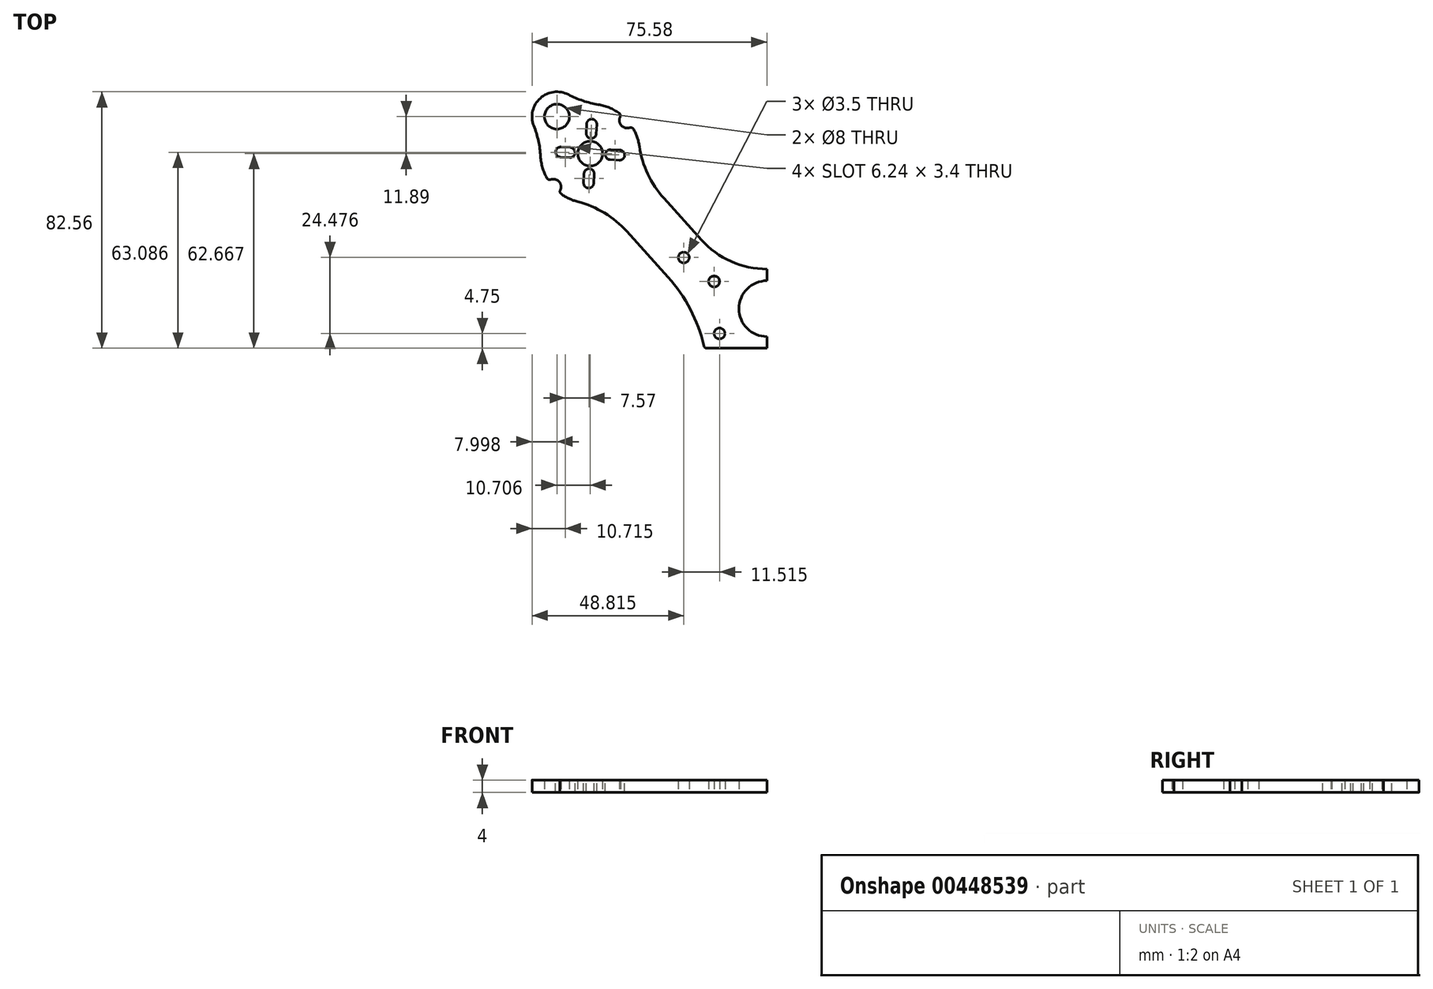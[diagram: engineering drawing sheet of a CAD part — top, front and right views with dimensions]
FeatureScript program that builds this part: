
annotation { "Feature Type Name" : "Feature", "Feature Type Description" : "" }
export const myFeature = defineFeature(function(context is Context, id is Id, definition is map)
    precondition{}
    {
        {
            var Q0;
            Q0=qCreatedBy(makeId("Top.planeOp"),FACE);
            var sketch = newSketch(context, id + "F0", { "sketchPlane" : qUnion([Q0])});
            skLineSegment(sketch, "E0", {"start": v(0, 10) * mm, "end": v(-56.88, 73.17) * mm, "construction": true});
            skCircle(sketch, "E1", {"center": v(-17, 32) * mm, "radius": 1.75 * mm});
            skCircle(sketch, "E2", {"center": v(-15.25, 15.25) * mm, "radius": 1.75 * mm});
            skLineSegment(sketch, "E3", {"start": v(-45.07, 48.1) * mm, "end": v(-31.81, 33.37) * mm});
            skLineSegment(sketch, "E4", {"start": v(-33.18, 58.8) * mm, "end": v(-21.1, 45.4) * mm});
            skLineSegment(sketch, "E5", {"start": v(-19.32, 10.5) * mm, "end": v(0, 10.5) * mm});
            skArc(sketch, "E6", {"start": v(-41.05, 75.52) * mm, "mid": v(-41.75, 78.38) * mm, "end": v(-42.96, 81.06) * mm});
            skLineSegment(sketch, "E7.trimOffspring", {"start": v(-53.55, 57.52) * mm, "end": v(-53.55, 57.52) * mm});
            skCircle(sketch, "E8", {"center": v(-56.88, 73.17) * mm, "radius": 14 * mm, "construction": true});
            skCircle(sketch, "E9", {"center": v(-56.88, 73.17) * mm, "radius": 4 * mm});
            skCircle(sketch, "E10", {"center": v(-26.77, 39.73) * mm, "radius": 1.75 * mm});
            skArc(sketch, "E11", {"start": v(-20.3, 11.27) * mm, "mid": v(-24.65, 23.06) * mm, "end": v(-31.81, 33.37) * mm});
            skPoint(sketch, "E12.orphan", {"position": v(-19, 0) * mm});
            skArc(sketch, "E13", {"start": v(-21.1, 45.4) * mm, "mid": v(-11.55, 38.46) * mm, "end": v(0, 36) * mm});
            skLineSegment(sketch, "E14", {"start": v(0, 36) * mm, "end": v(0, 32.25) * mm});
            skArc(sketch, "E15", {"start": v(0, 32.25) * mm, "mid": v(-9, 23.25) * mm, "end": v(0, 14.25) * mm});
            skLineSegment(sketch, "E16.trimOffspring", {"start": v(0, 14.25) * mm, "end": v(0, 10.5) * mm});
            skPoint(sketch, "E17.visualSharp", {"position": v(-20.12, 10.5) * mm});
            skArc(sketch, "E17.filletArc", {"start": v(-20.3, 11.27) * mm, "mid": v(-19.94, 10.72) * mm, "end": v(-19.32, 10.5) * mm});
            skPoint(sketch, "E18.visualSharp", {"position": v(-41.66, 68.22) * mm});
            skArc(sketch, "E18.filletArc", {"start": v(-41.05, 75.52) * mm, "mid": v(-38.35, 66.58) * mm, "end": v(-33.18, 58.8) * mm});
            skPoint(sketch, "E19.visualSharp", {"position": v(-53.55, 57.52) * mm});
            skArc(sketch, "E19.filletArc", {"start": v(-45.07, 48.1) * mm, "mid": v(-52.26, 54.05) * mm, "end": v(-60.87, 57.67) * mm});
            skArc(sketch, "E20", {"start": v(-47.25, 84.94) * mm, "mid": v(-46.84, 82.2) * mm, "end": v(-44.16, 81.51) * mm});
            skArc(sketch, "E21", {"start": v(-66.5, 61.4) * mm, "mid": v(-66.9, 64.13) * mm, "end": v(-69.6, 64.82) * mm});
            skLineSegment(sketch, "E22", {"start": v(-56.88, 73.17) * mm, "end": v(-67.58, 85.06) * mm, "construction": true});
            skLineSegment(sketch, "E23", {"start": v(-56.88, 73.17) * mm, "end": v(-44.99, 83.87) * mm, "construction": true});
            skLineSegment(sketch, "E24", {"start": v(-56.88, 73.17) * mm, "end": v(-68.77, 62.46) * mm, "construction": true});
            skArc(sketch, "E25.trimOffspring", {"start": v(-47.57, 86.18) * mm, "mid": v(-50.77, 87.96) * mm, "end": v(-54.29, 88.96) * mm});
            skArc(sketch, "E26.trimOffspring", {"start": v(-72.85, 72.24) * mm, "mid": v(-72.22, 68.64) * mm, "end": v(-70.8, 65.27) * mm});
            skArc(sketch, "E27.trimOffspring", {"start": v(-66.18, 60.15) * mm, "mid": v(-63.64, 58.67) * mm, "end": v(-60.87, 57.67) * mm});
            skPoint(sketch, "E28.visualSharp", {"position": v(-70.29, 64.44) * mm});
            skArc(sketch, "E28.filletArc", {"start": v(-70.8, 65.27) * mm, "mid": v(-70.27, 64.83) * mm, "end": v(-69.6, 64.82) * mm});
            skPoint(sketch, "E29.visualSharp", {"position": v(-66.95, 60.74) * mm});
            skArc(sketch, "E29.filletArc", {"start": v(-66.5, 61.4) * mm, "mid": v(-66.57, 60.71) * mm, "end": v(-66.18, 60.15) * mm});
            skPoint(sketch, "E30.visualSharp", {"position": v(-46.8, 85.6) * mm});
            skArc(sketch, "E30.filletArc", {"start": v(-47.25, 84.94) * mm, "mid": v(-47.18, 85.62) * mm, "end": v(-47.57, 86.18) * mm});
            skPoint(sketch, "E31.visualSharp", {"position": v(-43.46, 81.9) * mm});
            skArc(sketch, "E31.filletArc", {"start": v(-42.96, 81.06) * mm, "mid": v(-43.48, 81.5) * mm, "end": v(-44.16, 81.51) * mm});
            skArc(sketch, "E32", {"start": v(-63.89, 92.15) * mm, "mid": v(-72.94, 91) * mm, "end": v(-75.02, 82.12) * mm});
            skPoint(sketch, "E33.visualSharp", {"position": v(-60.49, 88.75) * mm});
            skArc(sketch, "E33.filletArc", {"start": v(-63.89, 92.15) * mm, "mid": v(-59.21, 90.17) * mm, "end": v(-54.29, 88.96) * mm});
            skPoint(sketch, "E34.visualSharp", {"position": v(-72, 78.39) * mm});
            skArc(sketch, "E34.filletArc", {"start": v(-72.85, 72.24) * mm, "mid": v(-73.54, 77.27) * mm, "end": v(-75.02, 82.12) * mm});
            skCircle(sketch, "E35", {"center": v(-67.58, 85.06) * mm, "radius": 4 * mm});
            skCircle(sketch, "E36", {"center": v(0, 0) * mm, "radius": 92.67 * mm, "construction": true});
            skCircle(sketch, "E37", {"center": v(-56.88, 73.17) * mm, "radius": 51.25 * mm, "construction": true});
            skSolve(sketch);
        }
        {
            var Q0;
            Q0=makeQuery(id+"F0.imprint","IMPRINT",FACE,{"disambiguationData":[TD([[makeQuery(id+"F0.imprint","IMPRINT",EDGE,{"derivedFrom":sQuery(id+"F0.wireOp",EDGE,"E1")}),-1.0]])]});
            extrude(context, id + "F1", {"entities" : qUnion([Q0]), "depth" : 4 * mm});
        }
        {
            var Q0;
            Q0=makeQuery(id+"F1.opExtrude","CAP_FACE",FACE,{"disambiguationData":[OSD([sQuery(id+"F0.wireOp",EDGE,"E1"),sQuery(id+"F0.wireOp",EDGE,"E2"),sQuery(id+"F0.wireOp",EDGE,"E3"),sQuery(id+"F0.wireOp",EDGE,"E4"),sQuery(id+"F0.wireOp",EDGE,"E5"),sQuery(id+"F0.wireOp",EDGE,"E6"),sQuery(id+"F0.wireOp",EDGE,"E9"),sQuery(id+"F0.wireOp",EDGE,"E10"),sQuery(id+"F0.wireOp",EDGE,"E11"),sQuery(id+"F0.wireOp",EDGE,"E13"),sQuery(id+"F0.wireOp",EDGE,"E14"),sQuery(id+"F0.wireOp",EDGE,"E15"),sQuery(id+"F0.wireOp",EDGE,"E16.trimOffspring"),sQuery(id+"F0.wireOp",EDGE,"E17.filletArc"),sQuery(id+"F0.wireOp",EDGE,"E18.filletArc"),sQuery(id+"F0.wireOp",EDGE,"E19.filletArc"),sQuery(id+"F0.wireOp",EDGE,"XlwXw7Ia-4k9A-3DB6-GY0S-PxJLlph5xH7B"),sQuery(id+"F0.wireOp",EDGE,"E20"),sQuery(id+"F0.wireOp",EDGE,"E21"),sQuery(id+"F0.wireOp",EDGE,"E25.trimOffspring"),sQuery(id+"F0.wireOp",EDGE,"E26.trimOffspring"),sQuery(id+"F0.wireOp",EDGE,"E27.trimOffspring"),sQuery(id+"F0.wireOp",EDGE,"465da84a-1fcb-458c-8af7-43b6bd39abb9.filletArc"),sQuery(id+"F0.wireOp",EDGE,"546c875d-b3e8-496f-961f-fee2dbec4bf7.filletArc"),sQuery(id+"F0.wireOp",EDGE,"E28.filletArc"),sQuery(id+"F0.wireOp",EDGE,"E29.filletArc"),sQuery(id+"F0.wireOp",EDGE,"E30.filletArc"),sQuery(id+"F0.wireOp",EDGE,"E31.filletArc")])],"isStart":false});
            var sketch = newSketch(context, id + "F2", { "sketchPlane" : qUnion([Q0])});
            skLineSegment(sketch, "E38", {"start": v(-56.88, 73.17) * mm, "end": v(0, 10) * mm, "construction": true});
            skLineSegment(sketch, "E39", {"start": v(-56.88, 73.17) * mm, "end": v(-50.39, 72.83) * mm, "construction": true});
            skLineSegment(sketch, "E40", {"start": v(-50.39, 72.83) * mm, "end": v(-47.39, 72.67) * mm, "construction": true});
            skArc(sketch, "E41.0.startCap", {"start": v(-50.47, 71.2) * mm, "mid": v(-52, 72.91) * mm, "end": v(-50.3, 74.45) * mm});
            skArc(sketch, "E41.0.endCap", {"start": v(-47.3, 74.3) * mm, "mid": v(-45.77, 72.59) * mm, "end": v(-47.47, 71.05) * mm});
            skLineSegment(sketch, "E41.0.left", {"start": v(-50.3, 74.45) * mm, "end": v(-47.3, 74.3) * mm});
            skLineSegment(sketch, "E41.0.right", {"start": v(-50.47, 71.2) * mm, "end": v(-47.47, 71.05) * mm});
            skLineSegment(sketch, "E42.1.0", {"start": v(-58.16, 79.74) * mm, "end": v(-58, 82.74) * mm});
            skArc(sketch, "E42.1.1", {"start": v(-54.91, 79.57) * mm, "mid": v(-56.62, 78.04) * mm, "end": v(-58.16, 79.74) * mm});
            skLineSegment(sketch, "E42.1.2", {"start": v(-54.91, 79.57) * mm, "end": v(-54.76, 82.57) * mm});
            skArc(sketch, "E42.1.3", {"start": v(-58, 82.74) * mm, "mid": v(-56.3, 84.28) * mm, "end": v(-54.76, 82.57) * mm});
            skLineSegment(sketch, "E42.2.0", {"start": v(-63.45, 71.88) * mm, "end": v(-66.45, 72.04) * mm});
            skArc(sketch, "E42.2.1", {"start": v(-63.28, 75.13) * mm, "mid": v(-61.74, 73.42) * mm, "end": v(-63.45, 71.88) * mm});
            skLineSegment(sketch, "E42.2.2", {"start": v(-63.28, 75.13) * mm, "end": v(-66.28, 75.29) * mm});
            skArc(sketch, "E42.2.3", {"start": v(-66.45, 72.04) * mm, "mid": v(-67.99, 73.75) * mm, "end": v(-66.28, 75.29) * mm});
            skLineSegment(sketch, "E42.3.0", {"start": v(-55.6, 66.6) * mm, "end": v(-55.75, 63.6) * mm});
            skArc(sketch, "E42.3.1", {"start": v(-58.84, 66.76) * mm, "mid": v(-57.13, 68.3) * mm, "end": v(-55.6, 66.6) * mm});
            skLineSegment(sketch, "E42.3.2", {"start": v(-58.84, 66.76) * mm, "end": v(-59, 63.77) * mm});
            skArc(sketch, "E42.3.3", {"start": v(-55.75, 63.6) * mm, "mid": v(-57.46, 62.06) * mm, "end": v(-59, 63.77) * mm});
            skPoint(sketch, "E42.center", {"position": v(-56.88, 73.17) * mm});
            skSolve(sketch);
        }
        {
            var Q0;
            Q0=qSketchRegion(id+"F2",true);
            extrude(context, id + "F3", {"entities" : qUnion([Q0]), "operationType" : NewBodyOperationType.REMOVE, "oppositeDirection" : true, "depth" : 25 * mm});
        }
    });
